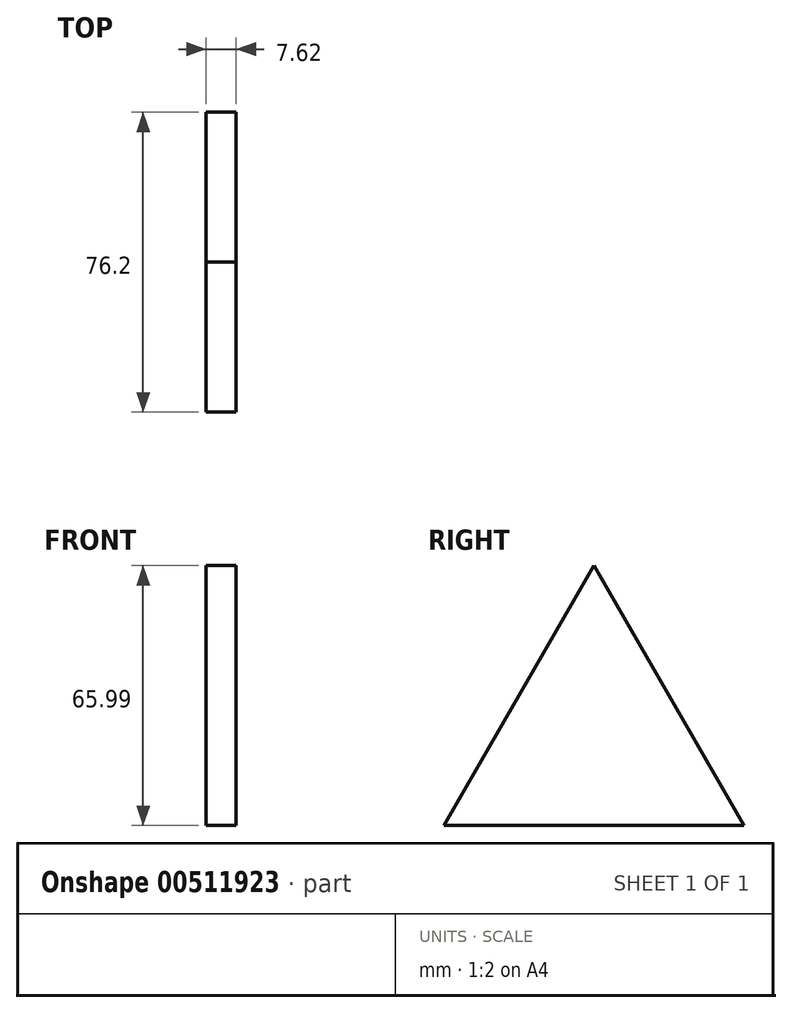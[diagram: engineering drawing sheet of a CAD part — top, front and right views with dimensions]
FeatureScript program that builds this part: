
annotation { "Feature Type Name" : "Feature", "Feature Type Description" : "" }
export const myFeature = defineFeature(function(context is Context, id is Id, definition is map)
    precondition{}
    {
        {
            var Q0;
            Q0=qCreatedBy(makeId("Right.planeOp"),FACE);
            var sketch = newSketch(context, id + "F0", { "sketchPlane" : qUnion([Q0])});
            skLineSegment(sketch, "E0", {"start": v(-0.55, 34.95) * mm, "end": v(-38.65, -31.04) * mm});
            skLineSegment(sketch, "E1", {"start": v(-38.65, -31.04) * mm, "end": v(37.55, -31.04) * mm});
            skLineSegment(sketch, "E2", {"start": v(37.55, -31.04) * mm, "end": v(-0.55, 34.95) * mm});
            skSolve(sketch);
        }
        {
            var Q0;
            Q0=makeQuery(id+"F0.imprint","IMPRINT",FACE,{"disambiguationData":[TD([[makeQuery(id+"F0.imprint","IMPRINT",EDGE,{"derivedFrom":sQuery(id+"F0.wireOp",EDGE,"E0")}),1.0]])]});
            extrude(context, id + "F1", {"entities" : qUnion([Q0]), "depth" : 7.62 * mm});
        }
    });
